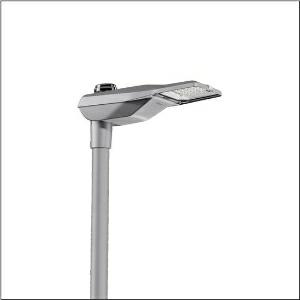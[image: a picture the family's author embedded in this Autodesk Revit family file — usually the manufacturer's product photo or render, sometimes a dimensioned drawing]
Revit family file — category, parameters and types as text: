
# Revit family: streetlight_sl_21_micro___st1_0a_5xe5d37n08cb_defe
name_source: partatom
category: Lighting Fixtures
units: mm (PartAtom-declared; Revit-internal decimal feet)

## family parameters
Cut with Voids When Loaded = No
Host = Face
Light Source = No
Part Type = Normal
Room Calculation Point = No
Round Connector Dimension = Use Diameter
Shared = No

## types (1)
- --- (1 x LED, 2290 lm, 15.8 W, 3000K)
    Apparent Load = 16 VA
    CIE Flux Codes = 37 72 97 100 100
    Color Rendering = 70
    Color Temperature = 3000K
    Default Elevation = 1800 mm
    Description = Streetlight SL 21 micro, mast luminaire, primary light control with lens, of PMMA, primary optical cover: cover, of toughened safety glass, transparent, light distribution: ST1.0a, light emission: direct distribution, primary light characteristic: asymmetric, installation type: post-top, LED, 3G 1.5mm², High Power LED, rated luminous flux: 2.290lm, luminous efficacy: 145lm/W, light colour: 730, colour temperature: 3000K, control gear: NEMA (7pin), control: overheat protection, pre-setting: linear dimming characteristic, constant luminous flux control, time-dependent luminous flux control, flexible luminous flux parameterisation, mains connection: 230..240V, AC, 50/60Hz, connection cable pre-assembled, cable length: 6,5m, wiring characteristics: H07RN-F, start of lifetime: 16W, end of service life: 16W, reduction: 8W, luminaire housing, of diecast aluminium (EN AC-44300), powder-coated, Siteco® metallic grey (DB 702S), corrosivity category C5 mid according to DIN EN ISO 12944, multi-level sealing system, sealing non-destructively replaceable, inclination adjustable: 0°, 5°, 10°, 15°, length: 528mm, width: 235mm, height: 110mm, spigot size: 76/60mm (post-top), mounting height: 4..8m, protection rating (complete): IP66, insulation class (complete): insulation class I (protective earthing), certification: CE, ENEC, ENEC+, VDE, impact resistance: IK10, permissible operating ambient temperature for outdoor applications: -40..+50°C, standard-compliant lighting for roads and squares, packaging unit: 1 piece

Light Distribution: ST1.0a
    Height = 110 mm
    Lamp = 1 x LED
    Lamp Light Flux = 2290 lm
    Lamp Power = 15.8 W
    Lamp count = 1
    Length = 528 mm
    Luminous efficacy = 145 lm/W
    Manufacturer = Siteco
    ModVariant = No
    Model = 5XE5D37N08CB
    Number of Poles = 1
    OnlyDefault = Yes
    Power Factor = 1
    Product Name = Streetlight SL 21 micro | ST1.0a
    Product group = mast luminaire | pylon top
    ProductGroupID = 6100
    Protection Class = Protection class I
    Protection Degree = IP 66
    RLX_Detail_Level = 1
    RLX_Emergency_Light_Flux = 0 lm
    RLX_Emergency_Type = 0
    RLX_Emergency_Type_DB = No
    RlxData = <blob elided: 98073 chars, md5=2aac1a39>
    Socket = socket
    Standby Power = 0 W
    System Light Flux = 2290 lm
    System Power = 16 W
    Type Comments = factory setting: luminous flux: 100 % | dim-lin: 254 | 300 mA
    Type Image = l_1294375.jpg
    URL = http://relux.com
    VarID = @adj_158063
    Voltage = 0 V
    Weight = 0.00 kg
    Width = 235 mm

## geometry (parser evidence)
native form markers: Blend x4, Sweep x11
no freeform markers — native parametric forms only
